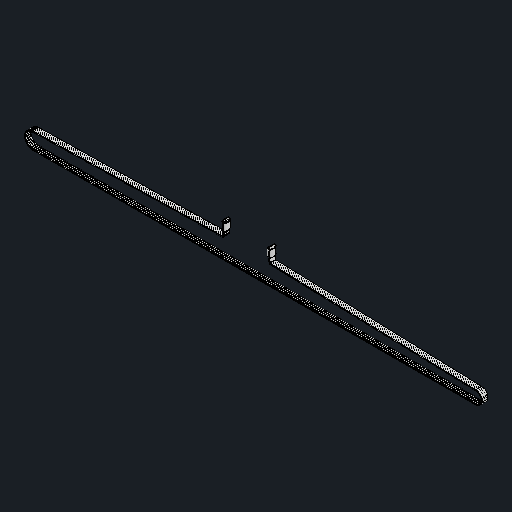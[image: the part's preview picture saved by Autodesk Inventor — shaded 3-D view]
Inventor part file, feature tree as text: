
AUTODESK INVENTOR PART (.ipt)
format: ipt  version: 2024.2 (Build 282272000, 272)  size: 1,923,072 bytes
history: native  units: mm
features: other x4, boolean_combine x1, mirror x1
ambient origin geometry x8: Origin, YZ Plane, XZ Plane, XY Plane, X Axis, Y Axis, Z Axis, Center Point
bodies: Body1 (feature_tree), Body2 (feature_tree), Body3 (feature_tree)
feature tree (6):
  other  "솔리드1"
  other  "솔리드2"
  other  "솔리드3"
  boolean_combine  "Combine1"
  mirror  "Mirror2"
  other  "Save Bodies1"
